# Revit family: Storage-Teknion-PLDLS_Lounge_Hieght_Drawer_Cabinet-R2015
name_source: partatom
category: Furniture
revit_build: Autodesk Revit Architecture 2015 (Build: 20140323_1530(x64)
units: mm (PartAtom-declared; Revit-internal decimal feet)

## types (2) — shared parameters
Assembly Code = E2020200
Height = 17.6 "
Manufacturer = Teknion
Manufacturer Fax = 416.661.4586
Part Number = PLDLS
Product Documentation Link = http://www.teknion.com
Product Line = Filing and Storage
Product Page URL = http://www.teknion.com
Series = Ledger Plus
Sustainability Data = http://www.teknion.com
URL = www.teknion.com
Unit Weight URL = http://www.teknion.com
Warranty = http://www.teknion.com

## per-type parameters (varying)
| type | Description | Model |
| Freestanding | Lounge Height Drawer Cabinet - Freestanding, Extra Large File | PLDLSFQ_ |
| Storage Supporting | Lounge Height Drawer Cabinet - Storage Supporting, Extra Large File | PLDLSSQ_ |

## geometry (parser evidence)
native form markers: Sweep x2
no freeform markers — native parametric forms only
